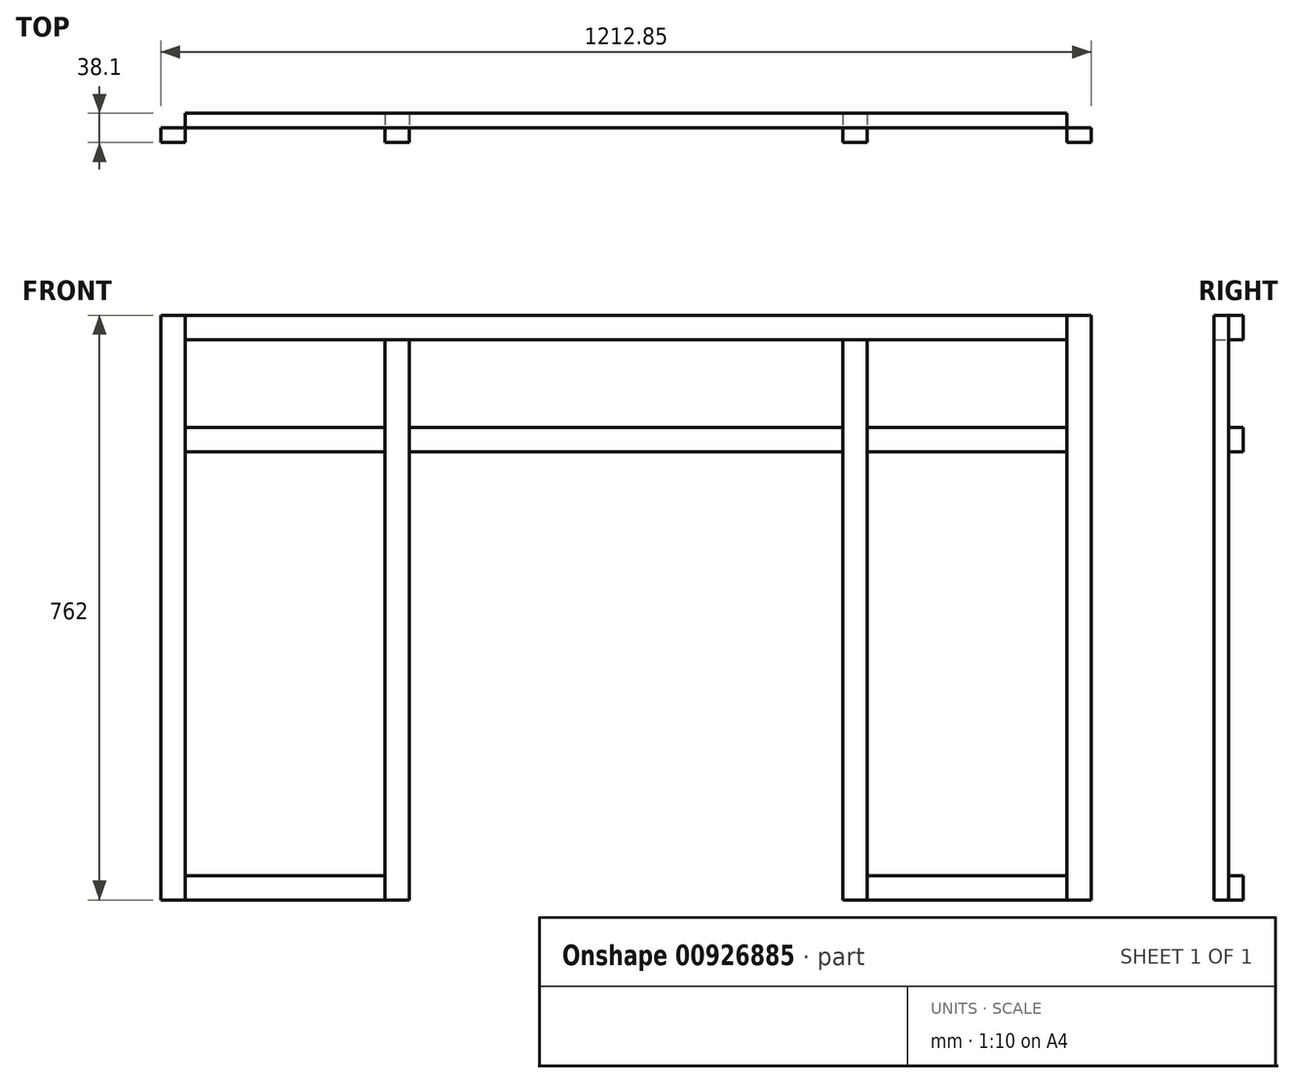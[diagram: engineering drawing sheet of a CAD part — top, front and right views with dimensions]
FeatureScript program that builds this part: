
annotation { "Feature Type Name" : "Feature", "Feature Type Description" : "" }
export const myFeature = defineFeature(function(context is Context, id is Id, definition is map)
    precondition{}
    {
        {
            var Q0;
            Q0=qCreatedBy(makeId("Front.planeOp"),FACE);
            var sketch = newSketch(context, id + "F0", { "sketchPlane" : qUnion([Q0])});
            skLineSegment(sketch, "E0.bottom", {"start": v(0, 0) * mm, "end": v(-323.85, 0) * mm});
            skLineSegment(sketch, "E0.top", {"start": v(0, 762) * mm, "end": v(-1212.85, 762) * mm});
            skLineSegment(sketch, "E0.left", {"start": v(0, 0) * mm, "end": v(0, 762) * mm});
            skLineSegment(sketch, "E0.right", {"start": v(-1212.85, 0) * mm, "end": v(-1212.85, 762) * mm});
            skLineSegment(sketch, "E1.0", {"start": v(-31.75, 730.25) * mm, "end": v(-1181.1, 730.25) * mm});
            skLineSegment(sketch, "E1.1", {"start": v(-31.75, 31.75) * mm, "end": v(-31.75, 730.25) * mm});
            skLineSegment(sketch, "E1.2", {"start": v(-31.75, 31.75) * mm, "end": v(-292.1, 31.75) * mm});
            skLineSegment(sketch, "E1.3", {"start": v(-1181.1, 31.75) * mm, "end": v(-1181.1, 730.25) * mm});
            skLineSegment(sketch, "E2", {"start": v(-1181.1, 730.25) * mm, "end": v(-1181.1, 762) * mm});
            skLineSegment(sketch, "E3", {"start": v(-1181.1, 31.75) * mm, "end": v(-1181.1, 0) * mm});
            skLineSegment(sketch, "E4", {"start": v(-31.75, 31.75) * mm, "end": v(-31.75, 0) * mm});
            skLineSegment(sketch, "E5", {"start": v(-31.75, 730.25) * mm, "end": v(-31.75, 762) * mm});
            skLineSegment(sketch, "E6.trimOffspring", {"start": v(-889, 0) * mm, "end": v(-1212.85, 0) * mm});
            skLineSegment(sketch, "E7.trimOffspring", {"start": v(-920.75, 31.75) * mm, "end": v(-1181.1, 31.75) * mm});
            skLineSegment(sketch, "E8.0", {"start": v(-330.2, 584.2) * mm, "end": v(-882.65, 584.2) * mm});
            skLineSegment(sketch, "E9.0", {"start": v(-330.2, 615.95) * mm, "end": v(-882.65, 615.95) * mm});
            skLineSegment(sketch, "E10.0", {"start": v(-31.75, 584.2) * mm, "end": v(-292.1, 584.2) * mm});
            skLineSegment(sketch, "E11.0", {"start": v(-31.75, 615.95) * mm, "end": v(-292.1, 615.95) * mm});
            skLineSegment(sketch, "E12.0", {"start": v(-920.75, 615.95) * mm, "end": v(-1181.1, 615.95) * mm});
            skLineSegment(sketch, "E13.0", {"start": v(-920.75, 584.2) * mm, "end": v(-1181.1, 584.2) * mm});
            skLineSegment(sketch, "E14.0", {"start": v(-889, 31.75) * mm, "end": v(-889, 730.25) * mm});
            skLineSegment(sketch, "E15.0", {"start": v(-920.75, 31.75) * mm, "end": v(-920.75, 730.25) * mm});
            skLineSegment(sketch, "E16.0", {"start": v(-323.85, 31.75) * mm, "end": v(-323.85, 730.25) * mm});
            skLineSegment(sketch, "E17.0", {"start": v(-292.1, 31.75) * mm, "end": v(-292.1, 730.25) * mm});
            skLineSegment(sketch, "E18", {"start": v(-882.65, 584.2) * mm, "end": v(-889, 584.2) * mm});
            skLineSegment(sketch, "E19", {"start": v(-882.65, 615.95) * mm, "end": v(-889, 615.95) * mm});
            skLineSegment(sketch, "E20", {"start": v(-330.2, 615.95) * mm, "end": v(-323.85, 615.95) * mm});
            skLineSegment(sketch, "E21", {"start": v(-330.2, 584.2) * mm, "end": v(-323.85, 584.2) * mm});
            skLineSegment(sketch, "E22", {"start": v(-292.1, 31.75) * mm, "end": v(-292.1, 0) * mm});
            skLineSegment(sketch, "E23", {"start": v(-323.85, 31.75) * mm, "end": v(-323.85, 0) * mm});
            skLineSegment(sketch, "E24", {"start": v(-920.75, 31.75) * mm, "end": v(-920.75, 0) * mm});
            skLineSegment(sketch, "E25", {"start": v(-889, 31.75) * mm, "end": v(-889, 0) * mm});
            skSolve(sketch);
        }
        {
            var Q0;
            {var subQ3=sQuery(id+"F0.wireOp",EDGE,"E0.right");Q0=makeQuery(id+"F0.imprint","IMPRINT",FACE,{"disambiguationData":[TD([[makeQuery(id+"F0.imprint","IMPRINT",EDGE,{"derivedFrom":subQ3}),-1.0]])]});}
            var Q1;
            {var subQ5=sQuery(id+"F0.wireOp",EDGE,"E24");Q1=makeQuery(id+"F0.imprint","IMPRINT",FACE,{"disambiguationData":[TD([[makeQuery(id+"F0.imprint","IMPRINT",EDGE,{"derivedFrom":subQ5}),1.0]])]});}
            var Q2;
            {var subQ9=sQuery(id+"F0.wireOp",EDGE,"E22");Q2=makeQuery(id+"F0.imprint","IMPRINT",FACE,{"disambiguationData":[TD([[makeQuery(id+"F0.imprint","IMPRINT",EDGE,{"derivedFrom":subQ9}),-1.0]])]});}
            var Q3;
            {var subQ0=sQuery(id+"F0.wireOp",EDGE,"E0.left");Q3=makeQuery(id+"F0.imprint","IMPRINT",FACE,{"disambiguationData":[TD([[makeQuery(id+"F0.imprint","IMPRINT",EDGE,{"derivedFrom":subQ0}),1.0]])]});}
            extrude(context, id + "F1", {"entities" : qUnion([Q0, Q1, Q2, Q3]), "depth" : 19.05 * mm, "offsetDistance" : 25.4 * mm});
        }
        {
            var Q0;
            {var subQ0=sQuery(id+"F0.wireOp",EDGE,"E3");Q0=makeQuery(id+"F0.imprint","IMPRINT",FACE,{"disambiguationData":[TD([[makeQuery(id+"F0.imprint","IMPRINT",EDGE,{"derivedFrom":subQ0}),1.0]])]});}
            var Q1;
            Q1=makeQuery(id+"F0.imprint","IMPRINT",FACE,{"disambiguationData":[TD([[makeQuery(id+"F0.imprint","IMPRINT",EDGE,{"derivedFrom":sQuery(id+"F0.wireOp",EDGE,"E1.2")}),1.0]])]});
            var Q2;
            Q2=makeQuery(id+"F0.imprint","IMPRINT",FACE,{"disambiguationData":[TD([[makeQuery(id+"F0.imprint","IMPRINT",EDGE,{"derivedFrom":sQuery(id+"F0.wireOp",EDGE,"E8.0")}),-1.0]])]});
            var Q3;
            {var subQ0=sQuery(id+"F0.wireOp",EDGE,"E12.0");Q3=makeQuery(id+"F0.imprint","IMPRINT",FACE,{"disambiguationData":[TD([[makeQuery(id+"F0.imprint","IMPRINT",EDGE,{"derivedFrom":subQ0}),1.0]])]});}
            var Q4;
            {var subQ5=sQuery(id+"F0.wireOp",EDGE,"E2");Q4=makeQuery(id+"F0.imprint","IMPRINT",FACE,{"disambiguationData":[TD([[makeQuery(id+"F0.imprint","IMPRINT",EDGE,{"derivedFrom":subQ5}),-1.0]])]});}
            var Q5;
            {var subQ0=sQuery(id+"F0.wireOp",EDGE,"E10.0");Q5=makeQuery(id+"F0.imprint","IMPRINT",FACE,{"disambiguationData":[TD([[makeQuery(id+"F0.imprint","IMPRINT",EDGE,{"derivedFrom":subQ0}),-1.0]])]});}
            extrude(context, id + "F2", {"entities" : qUnion([Q0, Q1, Q2, Q3, Q4, Q5]), "oppositeDirection" : true, "depth" : 19.05 * mm, "offsetDistance" : 25.4 * mm});
        }
    });
